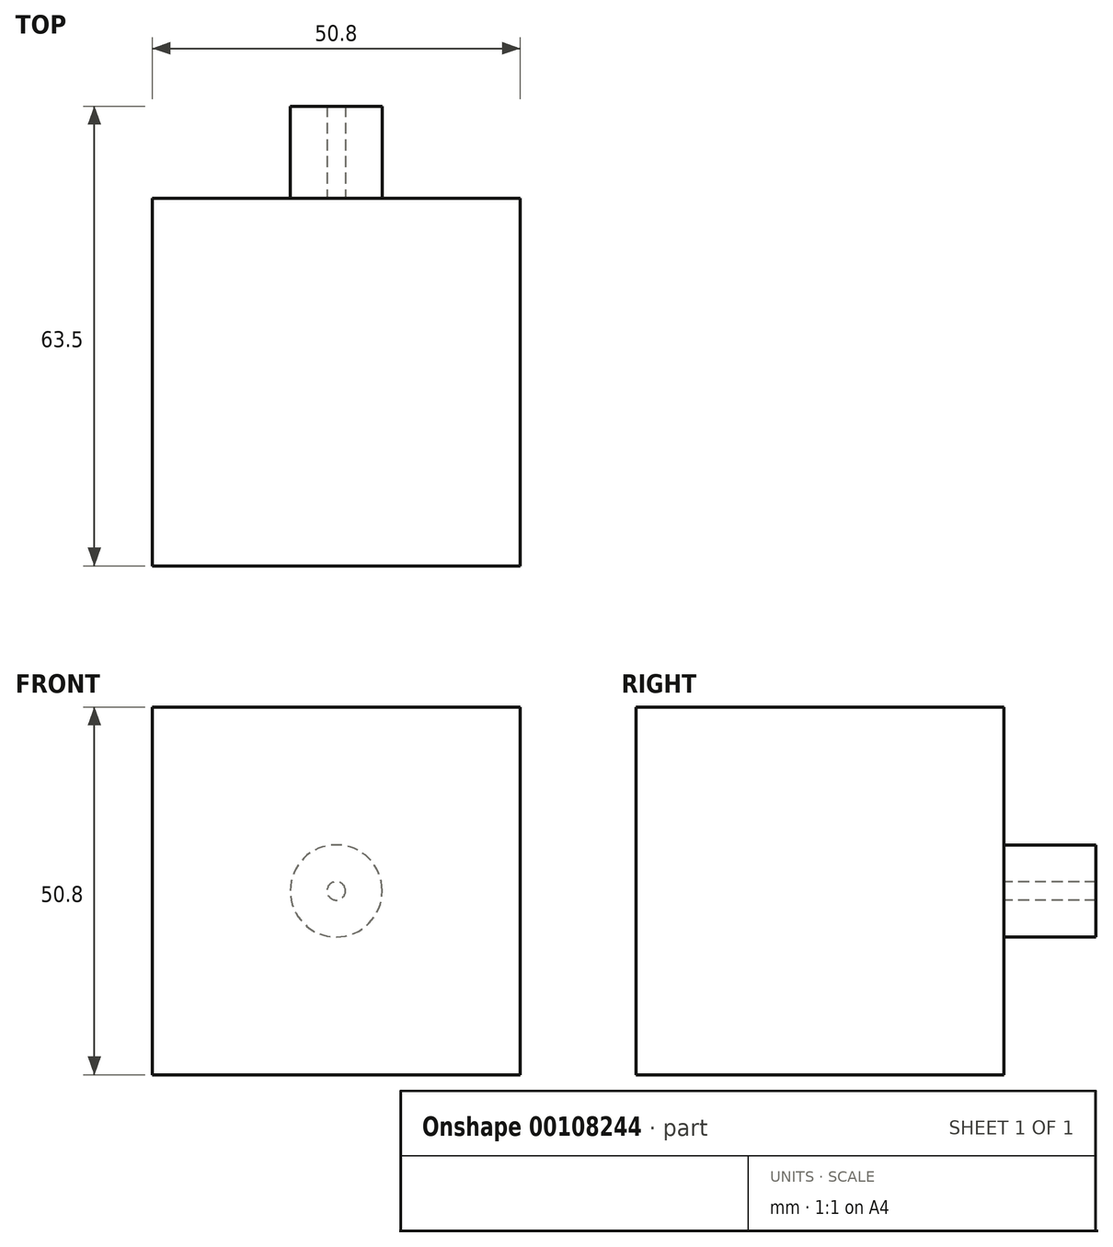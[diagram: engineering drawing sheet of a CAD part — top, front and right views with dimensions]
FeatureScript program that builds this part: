
annotation { "Feature Type Name" : "Feature", "Feature Type Description" : "" }
export const myFeature = defineFeature(function(context is Context, id is Id, definition is map)
    precondition{}
    {
        {
            var Q0;
            Q0=qCreatedBy(makeId("Front.planeOp"),FACE);
            var sketch = newSketch(context, id + "F0", { "sketchPlane" : qUnion([Q0])});
            skLineSegment(sketch, "E0.bottom", {"start": v(25.4, 25.4) * mm, "end": v(-25.4, 25.4) * mm});
            skLineSegment(sketch, "E0.top", {"start": v(25.4, -25.4) * mm, "end": v(-25.4, -25.4) * mm});
            skLineSegment(sketch, "E0.left", {"start": v(25.4, 25.4) * mm, "end": v(25.4, -25.4) * mm});
            skLineSegment(sketch, "E0.right", {"start": v(-25.4, 25.4) * mm, "end": v(-25.4, -25.4) * mm});
            skPoint(sketch, "E0.middle", {"position": v(0, 0) * mm});
            skSolve(sketch);
        }
        {
            var Q0;
            Q0=makeQuery(id+"F0.imprint","IMPRINT",FACE,{"disambiguationData":[TD([[makeQuery(id+"F0.imprint","IMPRINT",EDGE,{"derivedFrom":sQuery(id+"F0.wireOp",EDGE,"E0.bottom")}),1.0]])]});
            extrude(context, id + "F1", {"entities" : qUnion([Q0]), "depth" : 50.8 * mm});
        }
        {
            var Q0;
            Q0=makeQuery(id+"F1.opExtrude","CAP_FACE",FACE,{"disambiguationData":[OSD([sQuery(id+"F0.wireOp",EDGE,"E0.bottom"),sQuery(id+"F0.wireOp",EDGE,"E0.top"),sQuery(id+"F0.wireOp",EDGE,"E0.left"),sQuery(id+"F0.wireOp",EDGE,"E0.right")])],"isStart":true});
            var sketch = newSketch(context, id + "F2", { "sketchPlane" : qUnion([Q0])});
            skCircle(sketch, "E1", {"center": v(0, 0) * mm, "radius": 1.27 * mm});
            skCircle(sketch, "E2", {"center": v(0, 0) * mm, "radius": 6.35 * mm});
            skSolve(sketch);
        }
        {
            var Q0;
            Q0=makeQuery(id+"F2.imprint","IMPRINT",FACE,{"disambiguationData":[TD([[makeQuery(id+"F2.imprint","IMPRINT",EDGE,{"derivedFrom":sQuery(id+"F2.wireOp",EDGE,"E1")}),-1.0]])]});
            extrude(context, id + "F3", {"entities" : qUnion([Q0]), "operationType" : NewBodyOperationType.ADD, "depth" : 12.7 * mm});
        }
    });
